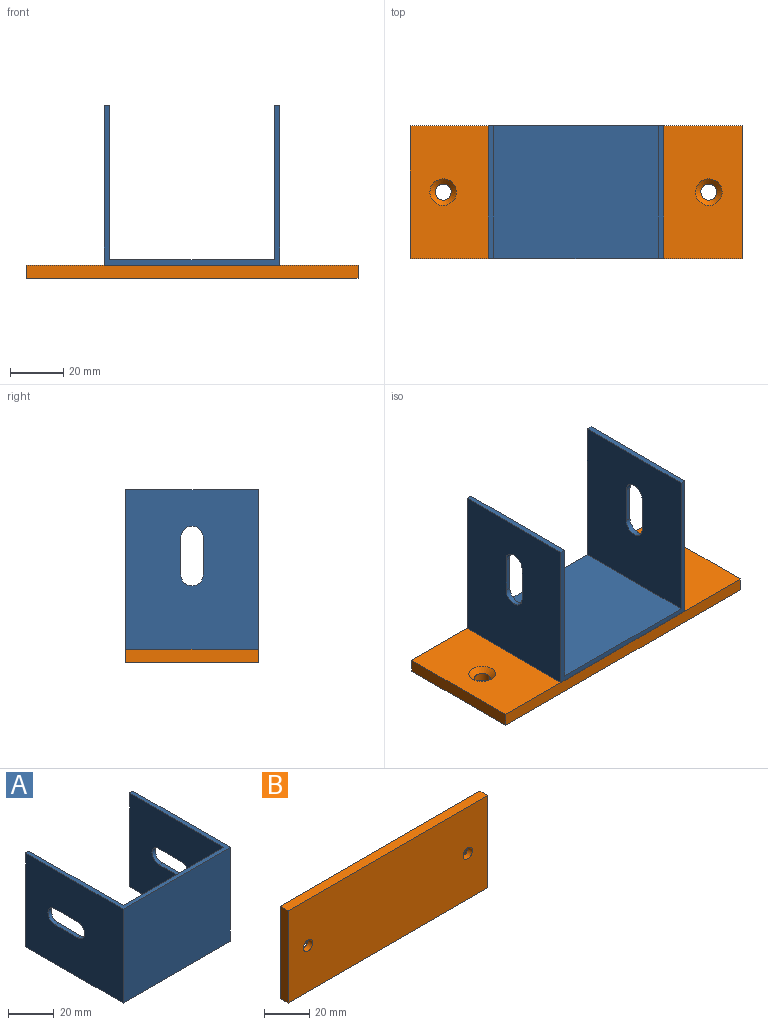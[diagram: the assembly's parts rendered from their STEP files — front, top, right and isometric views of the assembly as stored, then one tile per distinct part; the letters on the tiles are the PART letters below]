
ASSEMBLY  parts=2 mates=1
PART A: 18 faces, bbox 66x60x50 mm
  f0: plane 50x2mm, normal (0,1,0), area 100mm2, adj f1,f7,f8,f9
  f1: plane 60x50mm, normal (-1,0,0), area 2824.3mm2, adj f0,f2,f8,f9,f10,f11,f12,f13
  f2: plane 66x50mm, normal (0,-1,0), area 3300mm2, adj f1,f3,f8,f9
  f3: plane 60x50mm, normal (1,0,0), area 2824.3mm2, adj f2,f4,f8,f9,f14,f15,f16,f17
  f4: plane 50x2mm, normal (0,1,0), area 100mm2, adj f3,f5,f8,f9
  f5: plane 58x50mm, normal (-1,0,0), area 2724.3mm2, adj f4,f6,f8,f9,f14,f15,f16,f17
  f6: plane 62x50mm, normal (0,1,0), area 3100mm2, adj f5,f7,f8,f9
  f7: plane 58x50mm, normal (1,0,0), area 2724.3mm2, adj f0,f6,f8,f9,f10,f11,f12,f13
  f8: plane 66x60mm, normal (0,0,1), area 364mm2, adj f0,f1,f2,f3,f4,f5,f6,f7
  f9: plane 66x60mm, normal (0,0,-1), area 364mm2, adj f0,f1,f2,f3,f4,f5,f6,f7
  f10: plane 14x2mm, normal (0,0,-1), area 28mm2, adj f1,f7,f11,f13
  f11: cylinder r=4.25mm len=8.5mm, axis (1,0,0), area 26.7mm2, adj f1,f7,f10,f12
  f12: plane 14x2mm, normal (0,0,1), area 28mm2, adj f1,f7,f11,f13
  f13: cylinder r=4.25mm len=8.5mm, axis (1,0,0), area 26.7mm2, adj f1,f7,f10,f12
  f14: cylinder r=4.25mm len=8.5mm, axis (1,0,0), area 26.7mm2, adj f3,f5,f15,f17
  f15: plane 14x2mm, normal (0,0,1), area 28mm2, adj f3,f5,f14,f16
  f16: cylinder r=4.25mm len=8.5mm, axis (1,0,0), area 26.7mm2, adj f3,f5,f15,f17
  f17: plane 14x2mm, normal (0,0,-1), area 28mm2, adj f3,f5,f14,f16
PART B: 10 faces, bbox 125x5x50 mm
  f0: plane 125x5mm, normal (0,0,-1), area 625mm2, adj f1,f3,f4,f5
  f1: plane 50x5mm, normal (1,0,0), area 250mm2, adj f0,f2,f4,f5
  f2: plane 125x5mm, normal (0,0,1), area 625mm2, adj f1,f3,f4,f5
  f3: plane 50x5mm, normal (-1,0,0), area 250mm2, adj f0,f2,f4,f5
  f4: plane 125x50mm, normal (0,-1,0), area 6193.5mm2, adj f0,f1,f2,f3,f6,f7
  f5: plane 125x50mm, normal (0,1,0), area 6092.9mm2, adj f0,f1,f2,f3,f8,f9
  f6: cylinder r=3mm len=6mm, axis (0,1,0), area 56.5mm2, adj f4,f8
  f7: cylinder r=3mm len=6mm, axis (0,1,0), area 56.5mm2, adj f4,f9
  f8: cone r=3mm half-angle=45deg, axis (0,1,0), area 71.1mm2, adj f5,f6
  f9: cone r=3mm half-angle=45deg, axis (0,1,0), area 71.1mm2, adj f5,f7
PLACE A rot(axis=(1,0,0),90deg) t=(-14.51,18.61,22.19)mm
PLACE B rot(axis=(1,0,0),90deg) t=(16.49,-6.39,15.19)mm
MATE fastened A.f2 <-> B.f5  axis (0,0,-1) through (16.49,-6.39,20.19)mm
